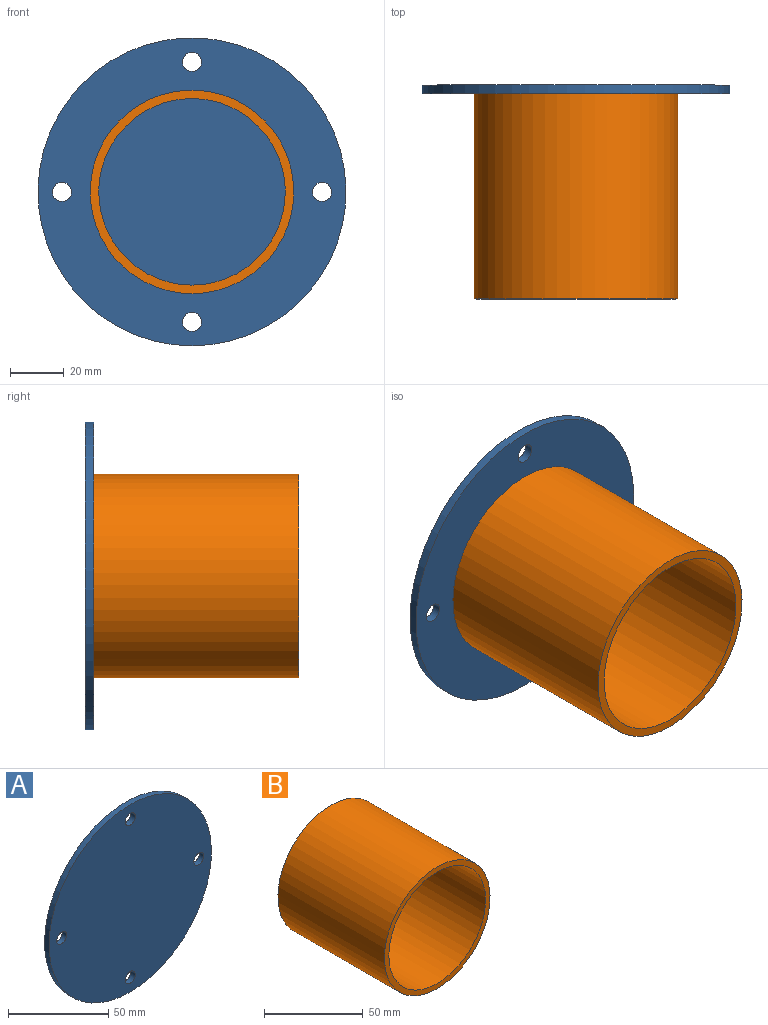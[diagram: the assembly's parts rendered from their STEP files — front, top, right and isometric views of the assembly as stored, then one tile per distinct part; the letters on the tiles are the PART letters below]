
ASSEMBLY  parts=2 mates=1
PART A: 7 faces, bbox 114.3x3.2x114.3 mm
  f0: cylinder r=3.56mm len=7.11mm, axis (0,1,0), area 70.9mm2, adj f5,f6
  f1: cylinder r=3.56mm len=7.11mm, axis (0,1,0), area 70.9mm2, adj f5,f6
  f2: cylinder r=3.56mm len=7.11mm, axis (0,1,0), area 70.9mm2, adj f5,f6
  f3: cylinder r=3.56mm len=7.11mm, axis (0,1,0), area 70.9mm2, adj f5,f6
  f4: cylinder r=57.15mm len=114.3mm, axis (0,1,0), area 1140.1mm2, adj f5,f6
  f5: plane 114.3x114.3mm, normal (0,-1,0), area 10101.9mm2, adj f0,f1,f2,f3,f4
  f6: plane 114.3x114.3mm, normal (0,1,0), area 10101.9mm2, adj f0,f1,f2,f3,f4
PART B: 4 faces, bbox 75.6x76.2x75.6 mm
  f0: cylinder r=34.61mm len=76.2mm, axis (0,1,0), area 16569.3mm2, adj f2,f3
  f1: cylinder r=37.78mm len=76.2mm, axis (0,1,0), area 18089.5mm2, adj f2,f3
  f2: plane 75.57x75.57mm, normal (0,-1,0), area 722.1mm2, adj f0,f1
  f3: plane 75.57x75.57mm, normal (0,1,0), area 722.1mm2, adj f0,f1
PLACE A at identity
PLACE B t=(69.4,-3.17,101.82)mm
MATE cylindrical B.f0 <-> A.f4  axis (0,1,0) through (0,-3.18,0)mm
